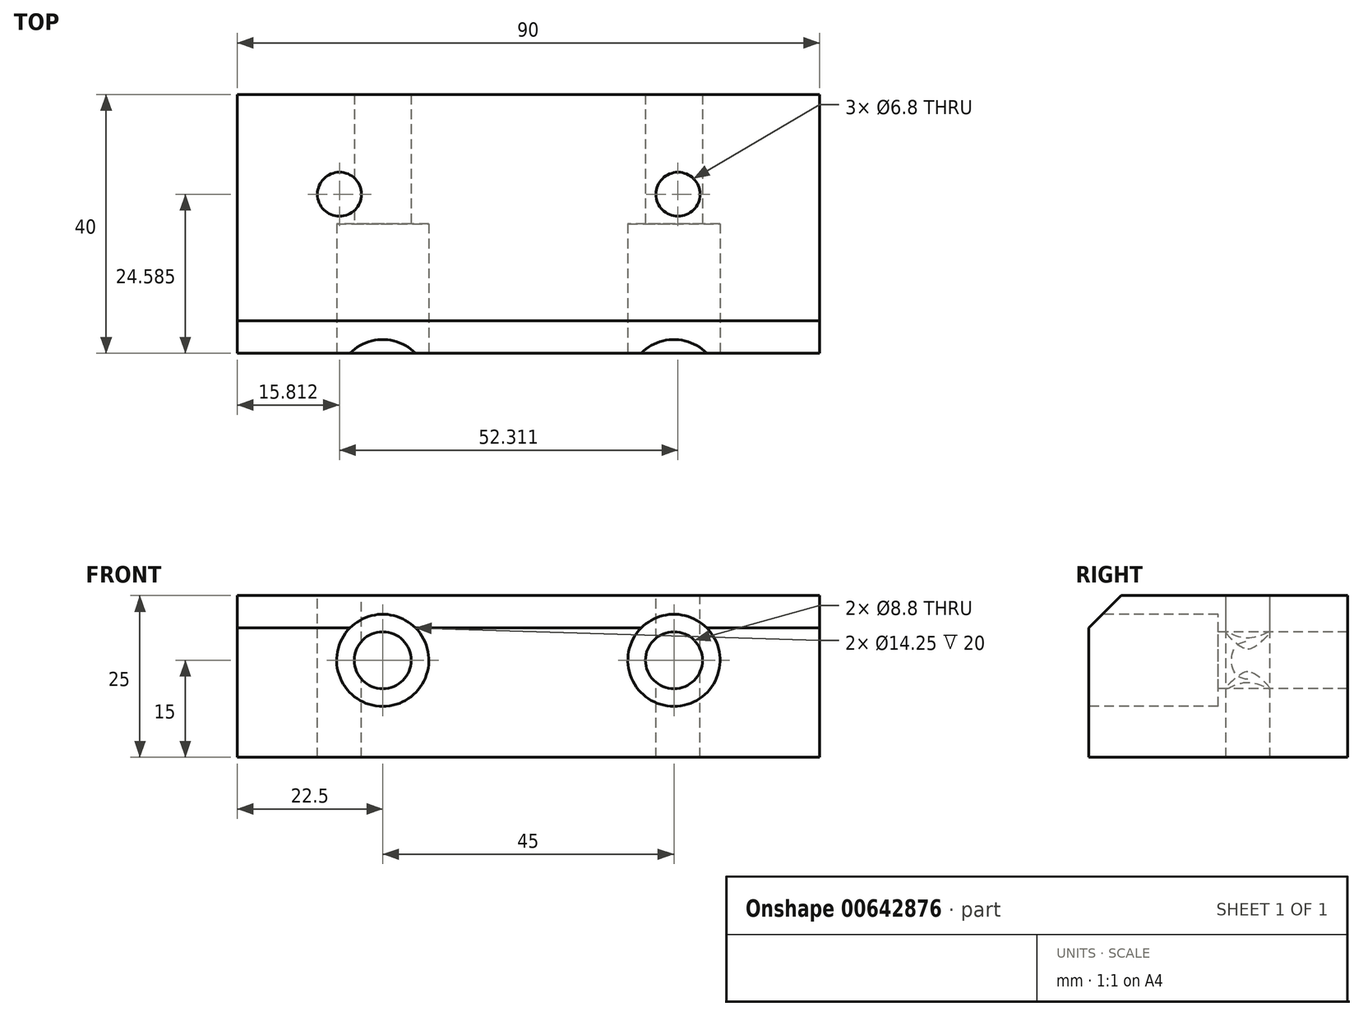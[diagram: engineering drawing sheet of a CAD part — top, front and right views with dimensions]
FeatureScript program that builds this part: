
annotation { "Feature Type Name" : "Feature", "Feature Type Description" : "" }
export const myFeature = defineFeature(function(context is Context, id is Id, definition is map)
    precondition{}
    {
        {
            var Q0;
            Q0=qCreatedBy(makeId("Front.planeOp"),FACE);
            var sketch = newSketch(context, id + "F0", { "sketchPlane" : qUnion([Q0])});
            skLineSegment(sketch, "E0.bottom", {"start": v(0, 0) * mm, "end": v(90, 0) * mm});
            skLineSegment(sketch, "E0.top", {"start": v(0, 25) * mm, "end": v(90, 25) * mm});
            skLineSegment(sketch, "E0.left", {"start": v(0, 0) * mm, "end": v(0, 25) * mm});
            skLineSegment(sketch, "E0.right", {"start": v(90, 0) * mm, "end": v(90, 25) * mm});
            skSolve(sketch);
        }
        {
            var Q0;
            Q0=makeQuery(id+"F0.imprint","IMPRINT",FACE,{"disambiguationData":[TD([[makeQuery(id+"F0.imprint","IMPRINT",EDGE,{"derivedFrom":sQuery(id+"F0.wireOp",EDGE,"E0.bottom")}),1.0]])]});
            extrude(context, id + "F1", {"entities" : qUnion([Q0]), "depth" : 40 * mm, "offsetDistance" : 25 * mm});
        }
        {
            var Q0;
            Q0=makeQuery(id+"F1.opExtrude","CAP_FACE",FACE,{"disambiguationData":[OSD([sQuery(id+"F0.wireOp",EDGE,"E0.bottom"),sQuery(id+"F0.wireOp",EDGE,"E0.top"),sQuery(id+"F0.wireOp",EDGE,"E0.left"),sQuery(id+"F0.wireOp",EDGE,"E0.right")])],"isStart":false});
            var sketch = newSketch(context, id + "F2", { "sketchPlane" : qUnion([Q0])});
            skPoint(sketch, "E1", {"position": v(22.5, 15) * mm});
            skPoint(sketch, "E2", {"position": v(67.5, 15) * mm});
            skSolve(sketch);
        }
        {
            var Q0;
            Q0=sQuery(id+"F2.wireOp",VERTEX,"E1");
            var Q1;
            Q1=sQuery(id+"F2.wireOp",VERTEX,"E2");
            var Q2;
            Q2=makeQuery(id+"F1.opExtrude","SWEPT_BODY",BODY,{"disambiguationData":[OSD([sQuery(id+"F0.wireOp",EDGE,"E0.bottom"),sQuery(id+"F0.wireOp",EDGE,"E0.top"),sQuery(id+"F0.wireOp",EDGE,"E0.left"),sQuery(id+"F0.wireOp",EDGE,"E0.right")])]});
            hole(context, id + "F3", {"style" : HoleStyle.C_BORE, "endStyle" : HoleEndStyle.THROUGH, "holeDiameter" : 8.8 * mm, "cBoreDiameter" : 14.25 * mm, "cBoreDepth" : 20 * mm, "majorDiameter" : 5 * mm, "isTappedThrough" : true, "tappedDepth" : 14.5 * mm, "tapClearance" : 3, "startFromSketch" : true, "locations" : qUnion([Q0, Q1]), "scope" : qUnion([Q2])});
        }
        {
            var Q0;
            Q0=makeQuery(id+"F1.opExtrude","CAP_EDGE",EDGE,{"disambiguationData":[OSD([sQuery(id+"F0.wireOp",EDGE,"E0.top")])],"isStart":false});
            chamfer(context, id + "F4", {"entities" : qUnion([Q0]), "width" : 5 * mm, "tangentPropagation" : true});
        }
        {
            var Q0;
            Q0=makeQuery(id+"F1.opExtrude","SWEPT_FACE",FACE,{"disambiguationData":[OSD([sQuery(id+"F0.wireOp",EDGE,"E0.top")])]});
            var sketch = newSketch(context, id + "F5", { "sketchPlane" : qUnion([Q0])});
            skPoint(sketch, "E3", {"position": v(15.81, -15.42) * mm});
            skPoint(sketch, "E4", {"position": v(68.12, -15.42) * mm});
            skSolve(sketch);
        }
        {
            var Q0;
            Q0=sQuery(id+"F5.wireOp",VERTEX,"E3");
            var Q1;
            Q1=sQuery(id+"F5.wireOp",VERTEX,"E4");
            var Q2;
            Q2=makeQuery(id+"F1.opExtrude","SWEPT_BODY",BODY,{"disambiguationData":[OSD([sQuery(id+"F0.wireOp",EDGE,"E0.bottom"),sQuery(id+"F0.wireOp",EDGE,"E0.top"),sQuery(id+"F0.wireOp",EDGE,"E0.left"),sQuery(id+"F0.wireOp",EDGE,"E0.right")])]});
            hole(context, id + "F6", {"style" : HoleStyle.SIMPLE, "endStyle" : HoleEndStyle.THROUGH, "standardTappedOrClearance" : lookupTablePath({ "standard" : "ISO", "engagement" : "75%", "pitch" : "1.25 mm", "size" : "M8", "type" : "Tapped" }), "standardBlindInLast" : lookupTablePath({ "standard" : "ISO", "engagement" : "75%", "pitch" : "1.25 mm", "size" : "M8", "type" : "Tapped" }), "holeDiameter" : 6.8 * mm, "majorDiameter" : 8 * mm, "showTappedDepth" : true, "isTappedThrough" : true, "tappedDepth" : 14.5 * mm, "tapClearance" : 3, "startFromSketch" : true, "locations" : qUnion([Q0, Q1]), "scope" : qUnion([Q2])});
        }
    });
